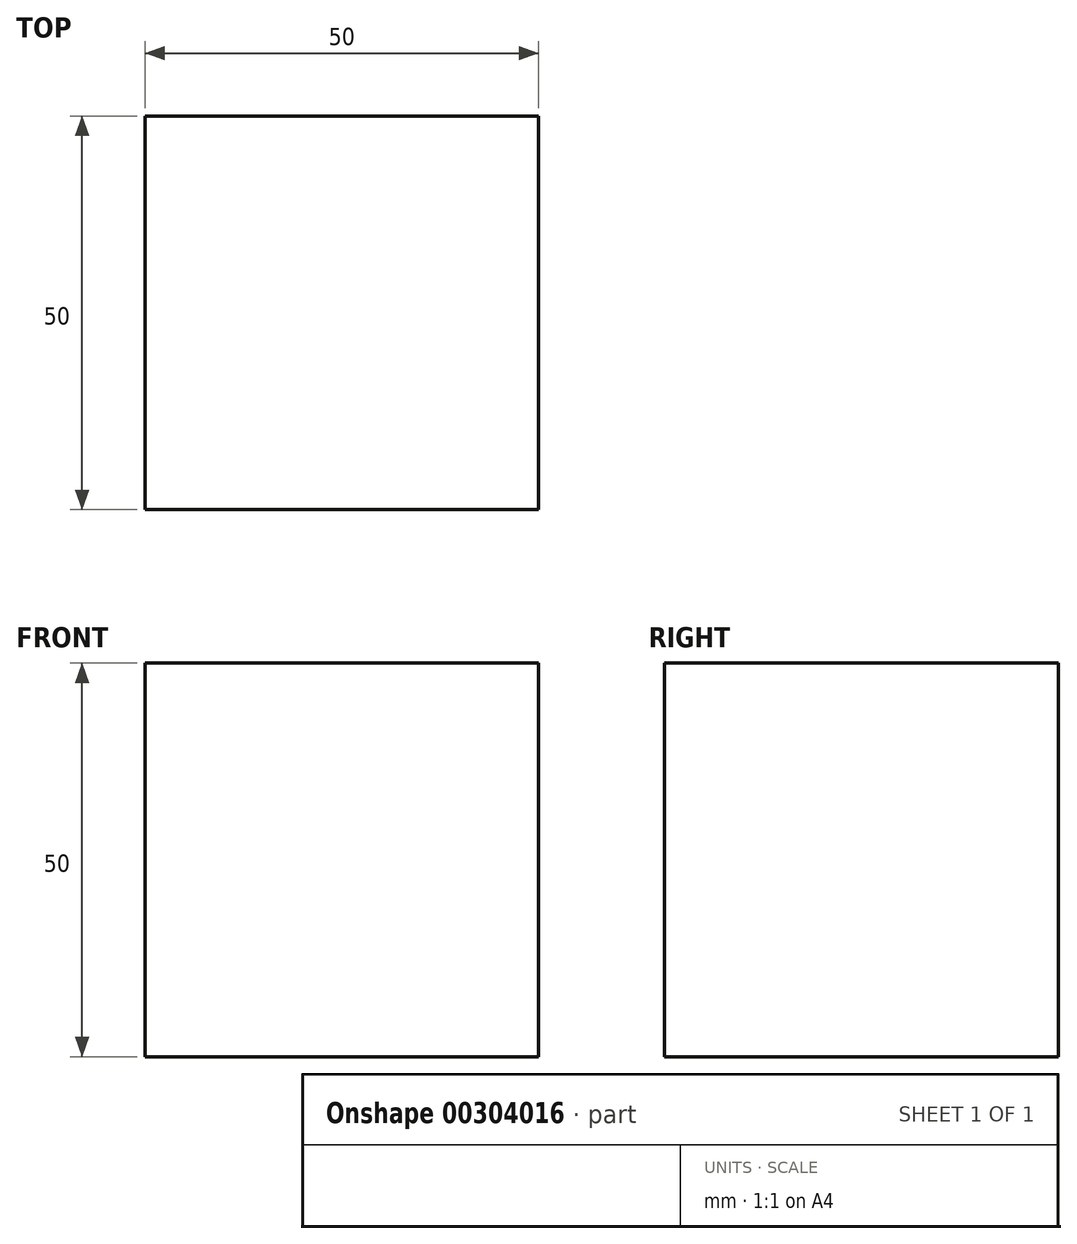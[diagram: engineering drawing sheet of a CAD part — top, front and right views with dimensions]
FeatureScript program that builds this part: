
annotation { "Feature Type Name" : "Feature", "Feature Type Description" : "" }
export const myFeature = defineFeature(function(context is Context, id is Id, definition is map)
    precondition{}
    {
        {
            var Q0;
            Q0=qCreatedBy(makeId("Front.planeOp"),FACE);
            var sketch = newSketch(context, id + "F0", { "sketchPlane" : qUnion([Q0])});
            skLineSegment(sketch, "E0.bottom", {"start": v(25, -25) * mm, "end": v(-25, -25) * mm});
            skLineSegment(sketch, "E0.top", {"start": v(25, 25) * mm, "end": v(-25, 25) * mm});
            skLineSegment(sketch, "E0.left", {"start": v(25, -25) * mm, "end": v(25, 25) * mm});
            skLineSegment(sketch, "E0.right", {"start": v(-25, -25) * mm, "end": v(-25, 25) * mm});
            skPoint(sketch, "E0.middle", {"position": v(0, 0) * mm});
            skSolve(sketch);
        }
        {
            var Q0;
            Q0 = qSketchRegion(id + "F0", true);
            extrude(context, id + "F1", {"entities" : qUnion([Q0]), "depth" : 25 * mm, "hasSecondDirection" : true, "secondDirectionOppositeDirection" : true, "secondDirectionDepth" : 25 * mm});
        }
    });
